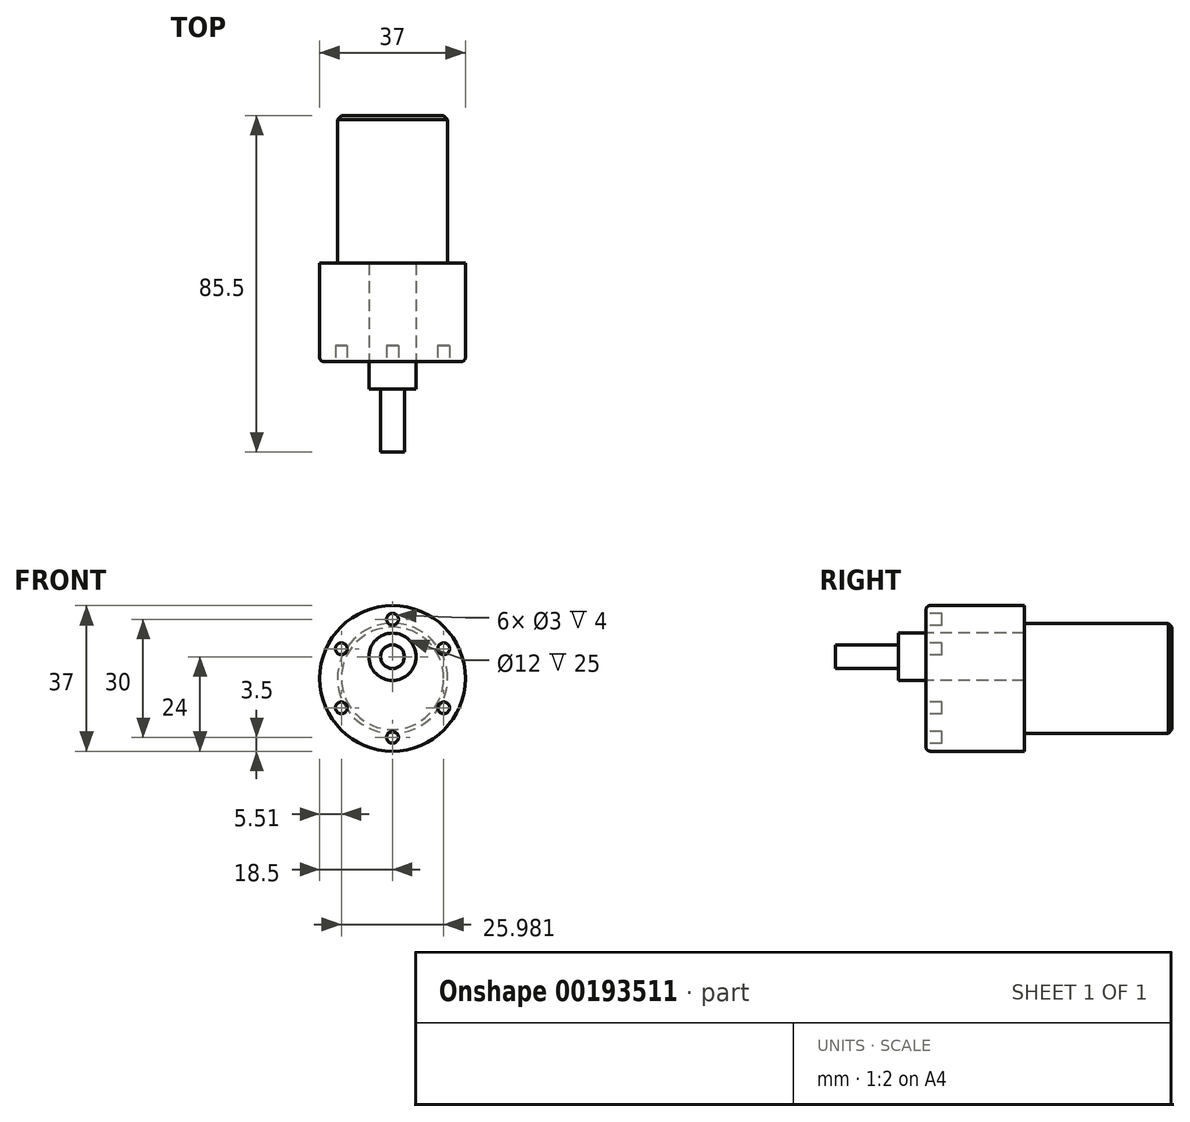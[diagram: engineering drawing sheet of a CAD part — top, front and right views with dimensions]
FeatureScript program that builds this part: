
annotation { "Feature Type Name" : "Feature", "Feature Type Description" : "" }
export const myFeature = defineFeature(function(context is Context, id is Id, definition is map)
    precondition{}
    {
        {
            var Q0;
            Q0=qCreatedBy(makeId("Front.planeOp"),FACE);
            var sketch = newSketch(context, id + "F0", { "sketchPlane" : qUnion([Q0])});
            skCircle(sketch, "E0", {"center": v(0, 0) * mm, "radius": 18.5 * mm});
            skCircle(sketch, "E1", {"center": v(0, 5.5) * mm, "radius": 6 * mm});
            skCircle(sketch, "E2", {"center": v(0, 5.5) * mm, "radius": 3 * mm});
            skSolve(sketch);
        }
        {
            var Q0;
            Q0=makeQuery(id+"F0.imprint","IMPRINT",FACE,{"disambiguationData":[TD([[makeQuery(id+"F0.imprint","IMPRINT",EDGE,{"derivedFrom":sQuery(id+"F0.wireOp",EDGE,"E2")}),1.0]])]});
            extrude(context, id + "F1", {"entities" : qUnion([Q0]), "depth" : 23 * mm});
        }
        {
            var Q0;
            Q0=makeQuery(id+"F0.imprint","IMPRINT",FACE,{"disambiguationData":[TD([[makeQuery(id+"F0.imprint","IMPRINT",EDGE,{"derivedFrom":sQuery(id+"F0.wireOp",EDGE,"E1")}),1.0]])]});
            extrude(context, id + "F2", {"entities" : qUnion([Q0]), "operationType" : NewBodyOperationType.ADD, "depth" : 7 * mm});
        }
        {
            var Q0;
            Q0=makeQuery(id+"F0.imprint","IMPRINT",FACE,{"disambiguationData":[TD([[makeQuery(id+"F0.imprint","IMPRINT",EDGE,{"derivedFrom":sQuery(id+"F0.wireOp",EDGE,"E0")}),1.0]])]});
            extrude(context, id + "F3", {"entities" : qUnion([Q0]), "operationType" : NewBodyOperationType.ADD, "oppositeDirection" : true, "depth" : 25 * mm});
        }
        {
            var Q0;
            Q0=makeQuery(id+"F3.opExtrude","CAP_FACE",FACE,{"disambiguationData":[OSD([sQuery(id+"F0.wireOp",EDGE,"E0"),sQuery(id+"F0.wireOp",EDGE,"E1")])],"isStart":false});
            var sketch = newSketch(context, id + "F4", { "sketchPlane" : qUnion([Q0])});
            skCircle(sketch, "E3", {"center": v(0, 0) * mm, "radius": 14 * mm});
            skSolve(sketch);
        }
        {
            var Q0;
            Q0 = qSketchRegion(id + "F4", true);
            extrude(context, id + "F5", {"entities" : qUnion([Q0]), "operationType" : NewBodyOperationType.ADD, "depth" : 37.5 * mm});
        }
        {
            var Q0;
            Q0=makeQuery(id+"F0.imprint","IMPRINT",FACE,{"disambiguationData":[TD([[makeQuery(id+"F0.imprint","IMPRINT",EDGE,{"derivedFrom":sQuery(id+"F0.wireOp",EDGE,"E0")}),1.0]])]});
            var sketch = newSketch(context, id + "F6", { "sketchPlane" : qUnion([Q0])});
            skCircle(sketch, "E4", {"center": v(0, 15) * mm, "radius": 1.5 * mm});
            skCircle(sketch, "E5.1.0", {"center": v(-13, 7.5) * mm, "radius": 1.5 * mm});
            skCircle(sketch, "E5.2.0", {"center": v(-13, -7.5) * mm, "radius": 1.5 * mm});
            skCircle(sketch, "E5.3.0", {"center": v(0, -15) * mm, "radius": 1.5 * mm});
            skCircle(sketch, "E5.4.0", {"center": v(13, -7.5) * mm, "radius": 1.5 * mm});
            skCircle(sketch, "E5.5.0", {"center": v(13, 7.5) * mm, "radius": 1.5 * mm});
            skPoint(sketch, "E5.center", {"position": v(0, 0) * mm});
            skSolve(sketch);
        }
        {
            var Q0;
            Q0 = qSketchRegion(id + "F6", true);
            extrude(context, id + "F7", {"entities" : qUnion([Q0]), "operationType" : NewBodyOperationType.REMOVE, "oppositeDirection" : true, "depth" : 4 * mm});
        }
        {
            var Q0;
            Q0=makeQuery(id+"F3.opExtrude","CAP_EDGE",EDGE,{"disambiguationData":[OSD([sQuery(id+"F0.wireOp",EDGE,"E0")])],"isStart":true});
            fillet(context, id + "F8", {"entities" : qUnion([Q0]), "radius" : 1 * mm, "tangentPropagation" : true, "allowEdgeOverflow" : false});
        }
        {
            var Q0;
            Q0=makeQuery(id+"F5.opExtrude","CAP_EDGE",EDGE,{"disambiguationData":[OSD([sQuery(id+"F4.wireOp",EDGE,"E3")])],"isStart":false});
            chamfer(context, id + "F9", {"entities" : qUnion([Q0]), "width" : 1 * mm, "tangentPropagation" : true});
        }
    });
